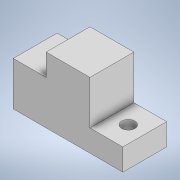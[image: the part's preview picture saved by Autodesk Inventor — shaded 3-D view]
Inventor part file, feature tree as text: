
AUTODESK INVENTOR PART (.ipt)
format: ipt  version: 2022 (Build 260153000, 153)  size: 110,080 bytes
history: native  units: mm
features: extrude x2, sketch x2, other x1
ambient origin geometry x8: Origin, YZ Plane, XZ Plane, XY Plane, X Axis, Y Axis, Z Axis, Center Point
bodies: Body1 (feature_tree)
feature tree (5):
  other  "Sólido1"
  extrude  "Extrusão1"  Depth=20.0mm
  extrude  "Extrusão2"  Depth=10.0mm
  sketch  "Esboço1"  dims[d0=50.0mm d1=20.0mm]
  sketch  "Esboço2"  dims[d2=15.0mm d3=10.0mm d4=20.0mm d5=20.0mm d6=15.0mm d7=20.0mm d8=0.0mm d9=6.0mm d10=7.5mm d11=10.0mm d12=0.0mm d13=0.0mm]
